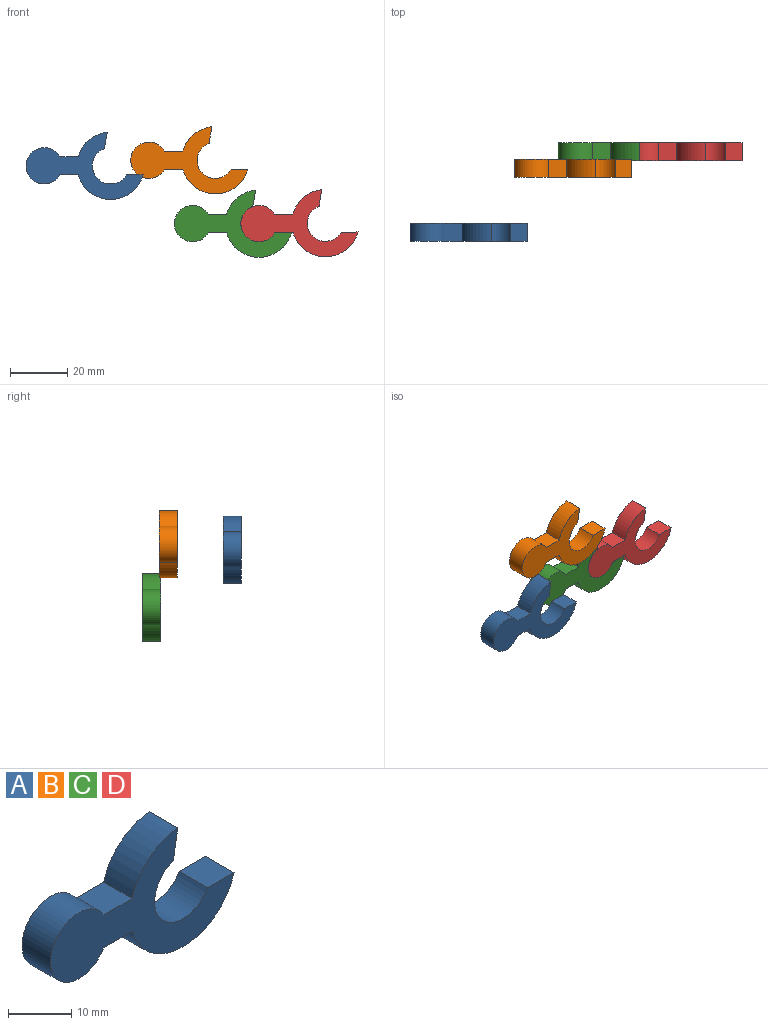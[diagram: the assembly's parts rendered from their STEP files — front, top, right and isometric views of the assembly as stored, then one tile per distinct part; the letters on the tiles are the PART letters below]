
ASSEMBLY  parts=4 mates=1
PART A: 10 faces, bbox 40.9x6.4x23.5 mm
  f0: cylinder r=6.35mm len=12.7mm, axis (0,1,0), area 211.1mm2, adj f1,f7,f8,f9
  f1: plane 6.35x6.35mm, normal (0,0,-1), area 40.3mm2, adj f0,f2,f8,f9
  f2: cylinder r=11.78mm len=22.68mm, axis (0,1,0), area 194.1mm2, adj f1,f3,f8,f9
  f3: plane 6.35x5.84mm, normal (0,0,1), area 37.1mm2, adj f2,f4,f8,f9
  f4: cylinder r=6.35mm len=12.31mm, axis (0,1,0), area 154.8mm2, adj f3,f5,f8,f9
  f5: plane 6.35x5.76mm, normal (0.99,0,-0.17), area 37.1mm2, adj f4,f6,f8,f9
  f6: cylinder r=11.78mm len=10.16mm, axis (0,1,0), area 89.6mm2, adj f5,f7,f8,f9
  f7: plane 6.35x6.35mm, normal (0,0,1), area 40.3mm2, adj f0,f6,f8,f9
  f8: plane 40.88x23.5mm, normal (0,-1,0), area 366.5mm2, adj f0,f1,f2,f3,f4,f5,f6,f7
  f9: plane 40.88x23.5mm, normal (0,1,0), area 366.5mm2, adj f0,f1,f2,f3,f4,f5,f6,f7
PART B: same geometry as A
PART C: same geometry as A
PART D: same geometry as A
PLACE A t=(-37.01,-7.26,24.31)mm
PLACE B t=(-0.45,15.13,26.24)mm
PLACE C t=(14.81,20.92,4.15)mm fixed
PLACE D rot(axis=(0,-1,0),0.4deg) t=(38,20.92,4.31)mm
MATE revolute C.f4 <-> D.f0  axis (0,1,0) through (14.81,17.75,4.15)mm
